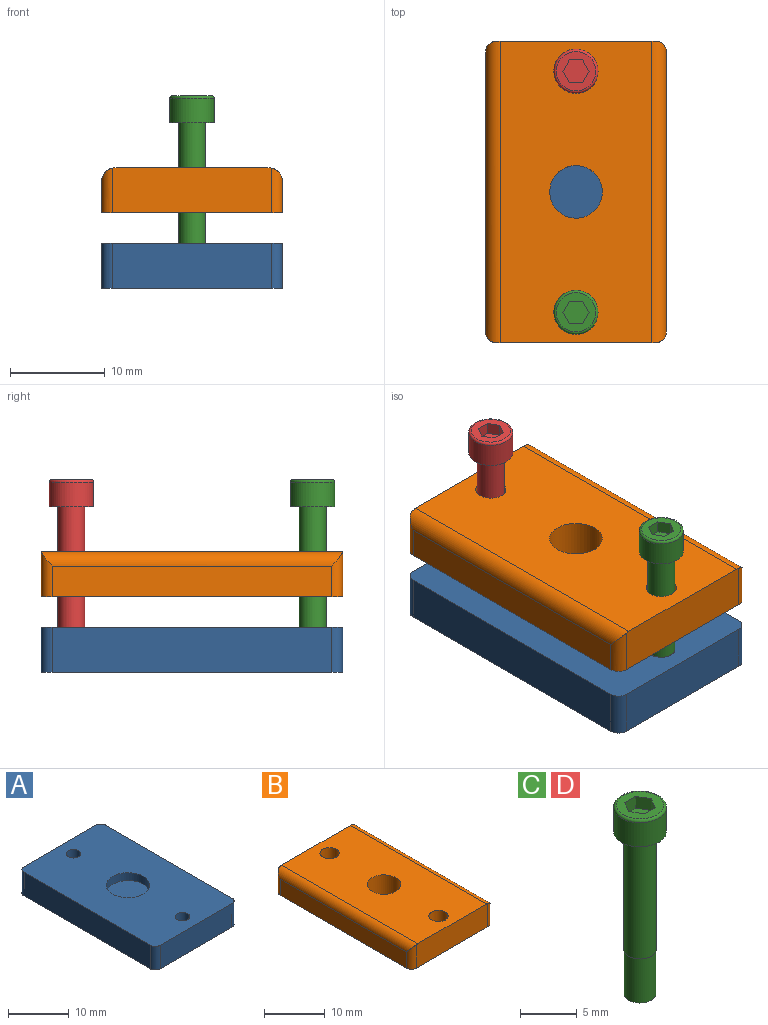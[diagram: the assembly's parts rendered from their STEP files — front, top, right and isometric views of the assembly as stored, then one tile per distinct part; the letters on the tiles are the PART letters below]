
ASSEMBLY  parts=4 mates=3
PART A: 14 faces, bbox 19.1x31.8x4.8 mm
  f0: plane 29.46x4.76mm, normal (1,0,0), area 140.3mm2, adj f1,f7,f8,f9
  f1: cylinder r=1.14mm len=4.76mm, axis (0,0,-1), area 8.6mm2, adj f0,f2,f8,f9
  f2: plane 16.76x4.76mm, normal (0,1,0), area 79.8mm2, adj f1,f3,f8,f9
  f3: cylinder r=1.14mm len=4.76mm, axis (0,0,-1), area 8.6mm2, adj f2,f4,f8,f9
  f4: plane 29.46x4.76mm, normal (-1,0,0), area 140.3mm2, adj f3,f5,f8,f9
  f5: cylinder r=1.14mm len=4.76mm, axis (0,0,-1), area 8.6mm2, adj f4,f6,f8,f9
  f6: plane 16.76x4.76mm, normal (0,-1,0), area 79.8mm2, adj f5,f7,f8,f9
  f7: cylinder r=1.14mm len=4.76mm, axis (0,0,-1), area 8.6mm2, adj f0,f6,f8,f9
  f8: plane 31.75x19.05mm, normal (0,0,1), area 554.6mm2, adj f0,f1,f2,f3,f4,f5,f6,f7
  f9: plane 31.75x19.05mm, normal (0,0,-1), area 594.6mm2, adj f0,f1,f2,f3,f4,f5,f6,f7
  f10: cylinder r=3.57mm len=7.14mm, axis (0,0,1), area 35.6mm2, adj f8,f11
  f11: plane 7.14x7.14mm, normal (0,0,1), area 40mm2, adj f10
  f12: cylinder r=1.21mm len=4.76mm, axis (0,0,1), area 36.1mm2, adj f8,f9
  f13: cylinder r=1.21mm len=4.76mm, axis (0,0,1), area 36.1mm2, adj f8,f9
PART B: 15 faces, bbox 19.1x31.8x4.8 mm
  f0: plane 29.46x3.24mm, normal (1,0,0), area 95.4mm2, adj f1,f8,f10,f14
  f1: cylinder r=1.14mm len=4.71mm, axis (0,0,-1), area 7.4mm2, adj f0,f2,f10,f14
  f2: plane 16.76x4.76mm, normal (0,1,0), area 79.8mm2, adj f1,f3,f9,f10,f13,f14
  f3: cylinder r=1.14mm len=4.71mm, axis (0,0,-1), area 7.4mm2, adj f2,f4,f10,f13
  f4: plane 29.46x3.24mm, normal (-1,0,0), area 95.4mm2, adj f3,f5,f10,f13
  f5: cylinder r=1.14mm len=4.71mm, axis (0,0,-1), area 7.4mm2, adj f4,f6,f10,f13
  f6: plane 16.76x4.76mm, normal (0,-1,0), area 79.8mm2, adj f5,f8,f9,f10,f13,f14
  f7: cylinder r=2.77mm len=5.54mm, axis (0,0,-1), area 82.9mm2, adj f9,f10
  f8: cylinder r=1.14mm len=4.71mm, axis (0,0,-1), area 7.4mm2, adj f0,f6,f10,f14
  f9: plane 31.75x16mm, normal (0,0,1), area 468.1mm2, adj f2,f6,f7,f11,f12,f13,f14
  f10: plane 31.75x19.05mm, normal (0,0,-1), area 563.7mm2, adj f0,f1,f2,f3,f4,f5,f6,f7
  f11: cylinder r=1.59mm len=4.76mm, axis (0,0,1), area 47.5mm2, adj f9,f10
  f12: cylinder r=1.59mm len=4.76mm, axis (0,0,1), area 47.5mm2, adj f9,f10
  f13: cylinder r=1.52mm len=31.75mm, axis (0,1,0), area 74.3mm2, adj f2,f3,f4,f5,f6,f9
  f14: cylinder r=1.52mm len=31.75mm, axis (0,-1,0), area 74.3mm2, adj f0,f1,f2,f6,f8,f9
PART C: 15 faces, bbox 5x5x20.3 mm
  f0: plane 4.14x4.14mm, normal (0,0,1), area 8.6mm2, adj f5,f6,f7,f8,f9,f10,f11
  f1: cylinder r=1.42mm len=12.7mm, axis (0,0,-1), area 113.5mm2, adj f2,f4
  f2: plane 2.85x2.85mm, normal (0,0,-1), area 0.2mm2, adj f1,f13
  f3: cylinder r=2.32mm len=4.65mm, axis (0,0,-1), area 37.8mm2, adj f4,f5
  f4: plane 4.65x4.65mm, normal (0,0,-1), area 10.6mm2, adj f1,f3
  f5: torus R=2.07mm, axis (0,0,1), area 5.6mm2, adj f0,f3
  f6: plane 1.37x1.27mm, normal (0,-1,0), area 1.7mm2, adj f0,f7,f11,f12
  f7: plane 1.27x1.19mm, normal (0.87,-0.5,0), area 1.7mm2, adj f0,f6,f8,f12
  f8: plane 1.27x1.19mm, normal (0.87,0.5,0), area 1.7mm2, adj f0,f7,f9,f12
  f9: plane 1.37x1.27mm, normal (0,1,0), area 1.7mm2, adj f0,f8,f10,f12
  f10: plane 1.27x1.19mm, normal (-0.87,0.5,0), area 1.7mm2, adj f0,f9,f11,f12
  f11: plane 1.27x1.19mm, normal (-0.87,-0.5,0), area 1.7mm2, adj f0,f6,f10,f12
  f12: plane 2.74x2.38mm, normal (0,0,1), area 4.9mm2, adj f6,f7,f8,f9,f10,f11
  f13: cylinder r=1.4mm len=4.75mm, axis (0,0,1), area 41.7mm2, adj f2,f14
  f14: plane 2.79x2.79mm, normal (0,0,-1), area 6.1mm2, adj f13
PART D: same geometry as C
PLACE A at identity fixed
PLACE B t=(0,0,7.95)mm
PLACE C t=(0,-12.7,4.75)mm
PLACE D t=(0,12.7,4.75)mm
MATE fastened D.f13 <-> A.f13  axis (0,0,-1) through (0,12.7,0)mm
MATE fastened C.f13 <-> A.f12  axis (0,0,-1) through (0,-12.7,0)mm
MATE slider B.f12 <-> A.f13  axis (0,0,1) through (0,12.7,12.71)mm
